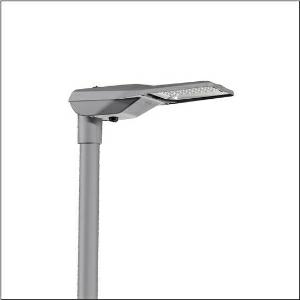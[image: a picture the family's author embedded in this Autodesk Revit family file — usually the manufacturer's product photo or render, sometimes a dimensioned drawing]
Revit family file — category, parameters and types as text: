
# Revit family: streetlight_sl_21_iq_mini___p0_8a_5xe2u31y08hb_44a6
name_source: partatom
category: Lighting Fixtures
units: mm (PartAtom-declared; Revit-internal decimal feet)

## family parameters
Cut with Voids When Loaded = No
Host = Face
Light Source = No
Part Type = Normal
Room Calculation Point = No
Round Connector Dimension = Use Diameter
Shared = No

## types (1)
- --- (1 x LED, 9830 lm, 71 W, 3000K)
    Apparent Load = 71 VA
    CIE Flux Codes = 33 69 96 100 100
    Color Rendering = 70
    Color Temperature = 3000K
    Default Elevation = 1800 mm
    Description = Streetlight SL 21 iQ mini, mast luminaire, primary light control with lens, of PMMA, primary optical cover: cover, of toughened safety glass, transparent, light distribution: P0.8a, light emission: direct distribution, primary light characteristic: asymmetric, installation type: post-top, side-entry, LED, High Power LED, rated luminous flux: 9.830lm, luminous efficacy: 139lm/W, light colour: 730, colour temperature: 3000K, control gear: iQ-Street Remote, D4i with power reduction, control: pre-setting: logarithmic dimming characteristic, Street-Remote, Auto-Match, Temp-Guard, Lumen-Switch, Night-Set, Smart-Wire, Light-Fading, Desk-Remote (wireless, voltage-free reading and setting of iQ features in the workshop via application-optimized NFC function/RFID function), optimised constant luminous flux control (CLO 2.0), mains connection: 220..240V, AC, 50/60Hz, start of lifetime: 71W, end of service life: 75W, reduction: 30W, luminaire housing, of diecast aluminium, powder-coated, Siteco® metallic grey (DB 702S), corrosivity category C5 mid according to DIN EN ISO 12944, please order mast flange separately, inclination adjustable: 0°, 5°, 10°, 15°, sealing non-destructively replaceable, multi-level sealing system, length: 628mm, width: 235mm, height: 110mm, mast flange for spigot size: 42mm (side-entry): 5XC10008XM4, 60/48mm (side-entry/post-top): 5XC10108XM2, 76/60mm (side-entry/post-top): 5XC10108XM1, mounting height: 4..8m, Smart Interface below and above, protection rating (complete): IP66, insulation class (complete): insulation class II (safety insulation), certification: CE, ENEC, ENEC+, VDE, impact resistance: IK10, permissible operating ambient temperature for outdoor applications: -40..+50°C, standard-compliant lighting for roads and squares, packaging unit: 1 piece

Light Distribution: P0.8a
    Height = 110 mm
    Lamp = 1 x LED
    Lamp Light Flux = 9830 lm
    Lamp Power = 71 W
    Lamp count = 1
    Length = 625 mm
    Luminous efficacy = 138 lm/W
    Manufacturer = Siteco
    ModVariant = No
    Model = 5XE2U31Y08HB
    Number of Poles = 1
    OnlyDefault = Yes
    Power Factor = 1
    Product Name = Streetlight SL 21 iQ mini | P0.8a
    Product group = mast luminaire | pylon top
    ProductGroupID = 6100
    Protection Class = Protection class II
    Protection Degree = IP 66
    RLX_Detail_Level = 1
    RLX_Emergency_Light_Flux = 0 lm
    RLX_Emergency_Type = 0
    RLX_Emergency_Type_DB = No
    RlxData = <blob elided: 92481 chars, md5=b1ab4d24>
    Socket = socket
    Standby Power = 0 W
    System Light Flux = 9830 lm
    System Power = 71 W
    Type Comments = factory setting: luminous flux: 100 % | dim-lin: 254 | 716 mA
    Type Image = l_1003514.jpg
    URL = http://relux.com
    VarID = @adj_095545
    Voltage = 0 V
    Weight = 0.00 kg
    Width = 234 mm

## geometry (parser evidence)
native form markers: Blend x4, Sweep x10
no freeform markers — native parametric forms only
